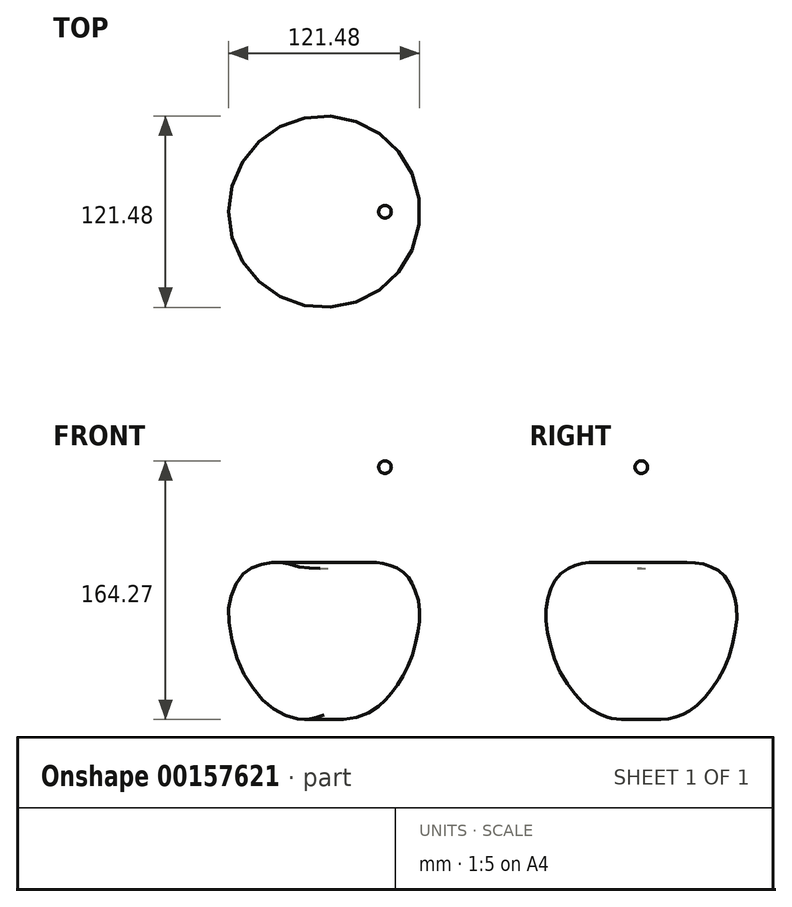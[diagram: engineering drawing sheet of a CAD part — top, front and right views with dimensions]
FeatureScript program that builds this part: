
annotation { "Feature Type Name" : "Feature", "Feature Type Description" : "" }
export const myFeature = defineFeature(function(context is Context, id is Id, definition is map)
    precondition{}
    {
        {
            var Q0;
            Q0=qCreatedBy(makeId("Front.planeOp"),FACE);
            var sketch = newSketch(context, id + "F0", { "sketchPlane" : qUnion([Q0])});
            skLineSegment(sketch, "E0", {"start": v(0, 46.03) * mm, "end": v(0, -47.02) * mm});
            skFitSpline(sketch, "E1", {"points": [v(0, -47.02) * mm, v(-4.72, -48.68) * mm, v(-11.16, -49.89) * mm, v(-20.41, -48.76) * mm, v(-33.29, -42.56) * mm, v(-45.44, -29.6) * mm, v(-55.66, -10.06) * mm, v(-60.67, 15.2) * mm, v(-59.28, 27.84) * mm, v(-53.56, 40.15) * mm, v(-46.56, 46.03) * mm, v(-37.95, 49) * mm, v(-30.15, 49.81) * mm, v(-25.24, 49.49) * mm, v(-18.16, 47.48) * mm, v(-9.15, 46.19) * mm, v(0, 46.03) * mm], "startDerivative": vector(-107.11, -40.82) * mm, "endDerivative": vector(158.94, 0.75) * mm});
            skSolve(sketch);
        }
        {
            var Q0;
            Q0=qCreatedBy(makeId("Front.planeOp"),FACE);
            var sketch = newSketch(context, id + "F1", { "sketchPlane" : qUnion([Q0])});
            skFitSpline(sketch, "E2", {"points": [v(0, 38.1) * mm, v(-8.09, 48.88) * mm, v(-13.12, 65.77) * mm, v(8.8, 85.18) * mm, v(29.65, 92) * mm, v(39.35, 104.94) * mm, v(38.64, 110.34) * mm], "startDerivative": vector(-52.4, 65.34) * mm, "endDerivative": vector(-18.56, 49.14) * mm});
            skCircle(sketch, "E3", {"center": v(38.64, 110.34) * mm, "radius": 4 * mm});
            skLineSegment(sketch, "E4", {"start": v(38.65, 114.34) * mm, "end": v(38.65, 106.34) * mm});
            skSolve(sketch);
        }
        {
            var Q0;
            Q0=qCreatedBy(makeId("Right.planeOp"),FACE);
            var sketch = newSketch(context, id + "F2", { "sketchPlane" : qUnion([Q0])});
            skFitSpline(sketch, "E5.0", {"points": [v(0, 24.12) * mm, v(0, 26.2) * mm, v(0, 30.67) * mm, v(0, 42.71) * mm, v(0, 55.96) * mm, v(0, 55.92) * mm, v(0, 66.17) * mm, v(0, 68.88) * mm, v(0, 69.87) * mm]});
            skCircle(sketch, "E6", {"center": v(0, 38.1) * mm, "radius": 4 * mm});
            skSolve(sketch);
        }
        {
            var Q0;
            Q0=makeQuery(id+"F0.imprint","IMPRINT",FACE,{"disambiguationData":[TD([[makeQuery(id+"F0.imprint","IMPRINT",EDGE,{"derivedFrom":sQuery(id+"F0.wireOp",EDGE,"E0")}),-1.0]])]});
            var Q1;
            Q1=sQuery(id+"F0.wireOp",EDGE,"E0");
            revolve(context, id + "F3", {"entities" : qUnion([Q0]), "axis" : qUnion([Q1]), "revolveType" : RevolveType.FULL});
        }
        {
            var Q0;
            {var subQ0=sQuery(id+"F1.wireOp",EDGE,"E3");var subQ1=sQuery(id+"F1.wireOp",EDGE,"E2");var subQ2=makeQuery(id+"F1.imprint","INTERSECT",VERTEX,{"derivedFrom":[subQ1,subQ0]});Q0=makeQuery(id+"F1.imprint","IMPRINT",FACE,{"disambiguationData":[TD([[makeQuery(id+"F1.imprint","IMPRINT",EDGE,{"disambiguationData":[TD([[subQ2,-1.0]])],"derivedFrom":subQ1}),-1.0]])]});}
            var Q1;
            {var subQ0=sQuery(id+"F1.wireOp",EDGE,"E3");var subQ1=sQuery(id+"F1.wireOp",EDGE,"E2");var subQ2=makeQuery(id+"F1.imprint","INTERSECT",VERTEX,{"derivedFrom":[subQ1,subQ0]});Q1=makeQuery(id+"F1.imprint","IMPRINT",FACE,{"disambiguationData":[TD([[makeQuery(id+"F1.imprint","IMPRINT",EDGE,{"disambiguationData":[TD([[subQ2,-1.0]])],"derivedFrom":subQ1}),1.0]])]});}
            var Q2;
            Q2=sQuery(id+"F1.wireOp",EDGE,"E4");
            revolve(context, id + "F4", {"operationType" : NewBodyOperationType.ADD, "entities" : qUnion([Q0, Q1]), "axis" : qUnion([Q2]), "revolveType" : RevolveType.FULL});
        }
    });
